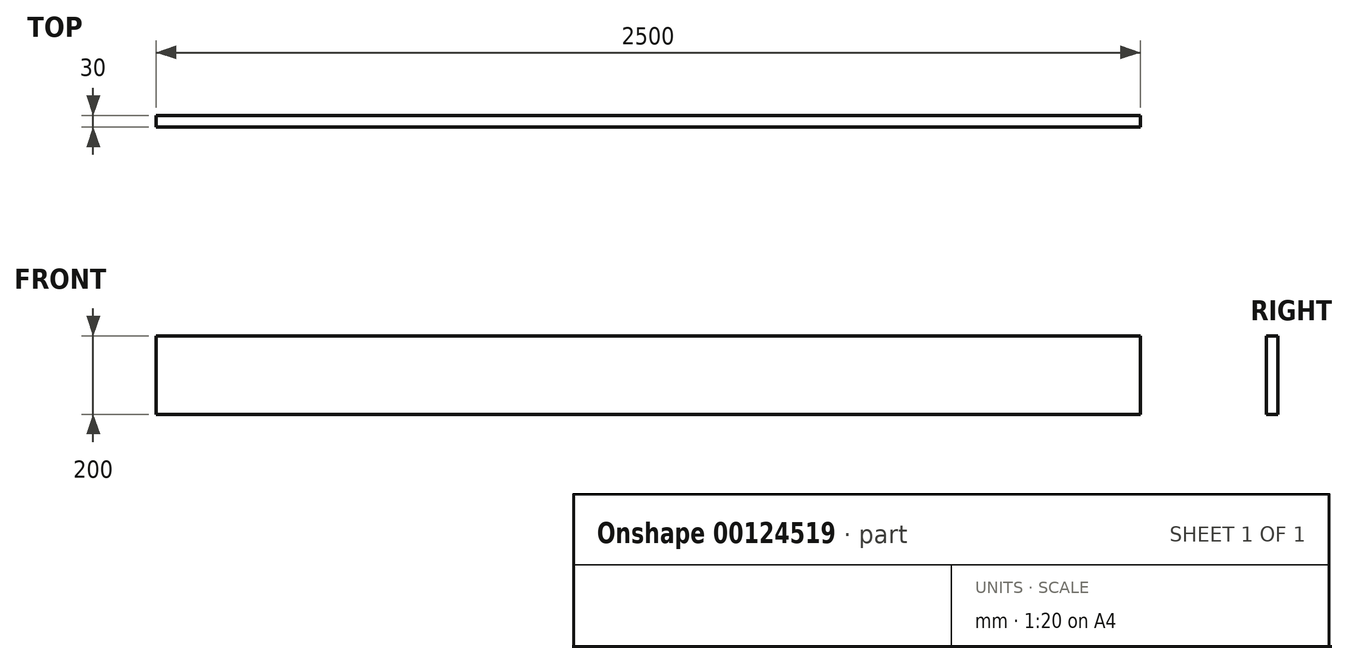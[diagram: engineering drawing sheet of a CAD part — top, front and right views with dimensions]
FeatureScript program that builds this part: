
annotation { "Feature Type Name" : "Feature", "Feature Type Description" : "" }
export const myFeature = defineFeature(function(context is Context, id is Id, definition is map)
    precondition{}
    {
        {
            var Q0;
            Q0=qCreatedBy(makeId("Front.planeOp"),FACE);
            var sketch = newSketch(context, id + "F0", { "sketchPlane" : qUnion([Q0])});
            skLineSegment(sketch, "E0.bottom", {"start": v(1250, 100) * mm, "end": v(-1250, 100) * mm});
            skLineSegment(sketch, "E0.top", {"start": v(1250, -100) * mm, "end": v(-1250, -100) * mm});
            skLineSegment(sketch, "E0.left", {"start": v(1250, 100) * mm, "end": v(1250, -100) * mm});
            skLineSegment(sketch, "E0.right", {"start": v(-1250, 100) * mm, "end": v(-1250, -100) * mm});
            skPoint(sketch, "E0.middle", {"position": v(0, 0) * mm});
            skSolve(sketch);
        }
        {
            var Q0;
            Q0 = qSketchRegion(id + "F0", true);
            extrude(context, id + "F1", {"entities" : qUnion([Q0]), "depth" : 30 * mm});
        }
    });
